# Revit family: Toilet_Seat-Elongated_Closed_Front-KOHLER-Cachet-K-4636T_1
name_source: partatom
category: Specialty Equipment
units: mm (PartAtom-declared; Revit-internal decimal feet)

## family parameters
Cut with Voids When Loaded = No
Host = Face
OmniClass Number = 23.31.19.19.17
OmniClass Title = Water Closet Seats
Part Type = Normal
Room Calculation Point = No
Round Connector Dimension = Use Diameter
Shared = No

## types (3) — shared parameters
ADA Compliant = No
Assembly Code = C1030200
Date Modified = 04/17/2023
Default Elevation = 15"
Description = Scratch-Resistant and Slowly Lowers The Toilet Seat
Height = 2 3/16"
Length = 19 5/8"
Manufacturer = Kohler Co.
Master Format 2014 = 10 28 00
Master Format 2014 Name = Toilet, Bath, and Laundry Accessories
Material = Plastic
Product Documentation Link = https://files.kohler.com.cn
Product Name = Cachet
URL = http://www.kohler.com.cn
WaterSense Certified = No
Width = 14 3/16"

## per-type parameters (varying)
| type | Finish | Model | Product Page URL | Type |
| 0-White | Kohler-Plastic-0-White | K-4636T-U-0 | https://www.kohler.com.cn | 1 |
| 47-Almond | Kohler-Plastic-47-Almond | K-4636T-U-47 |  | 2 |
| 96-Biscuit | Kohler-Plastic-96-Biscuit | K-4636T-U-96 |  | 3 |

## geometry (parser evidence)
native form markers: Sweep x4
no freeform markers — native parametric forms only
